FCSTD DOCUMENT  (FreeCAD 0.14R3703 (Git))
Label: halfHullS
License: CC-BY 3.0
LicenseURL: http://creativecommons.org/licenses/by/3.0/
objects: Sketcher::SketchObject×12, App::DocumentObjectGroup×1
note: 12 computed .brp shape members not serialized (recipe doc carries the construction recipe); baked Part::Feature solids carry a one-line shape summary decoded from their .brp

FEATURE [Sketcher::SketchObject] Sketch044  label="transomXY"
  sketch-geometry (3):
    g0: LineSegment StartX=0.095576 StartY=-850 StartZ=0 EndX=46.3737 EndY=-848.446 EndZ=0
    g1: LineSegment StartX=46.3737 StartY=-848.446 StartZ=0 EndX=77.9269 EndY=-843.772 EndZ=0
    g2: LineSegment StartX=77.9269 StartY=-843.772 StartZ=0 EndX=100 EndY=-839 EndZ=0
  constraints (5):
    c: Coincident(g0,g1)
    c: Coincident(g1,g2)
    c: DistanceY(g-1,g0) = -850
    c: DistanceY(g-1,g2) = -839
    c: DistanceX(g-1,g2) = 100
FEATURE [Sketcher::SketchObject] Sketch045  label="transom corners sketch"
  Placement = pos=(0,-828,43) rot=(1,0,0;1.71042rad)
  sketch-geometry (3):
    g0: LineSegment StartX=0 StartY=-34.8021 StartZ=0 EndX=45.4 EndY=-31.2923 EndZ=0
    g1: LineSegment StartX=45.4 StartY=-31.2923 StartZ=0 EndX=76.2 EndY=4.1704 EndZ=0
    g2: LineSegment StartX=76.2 StartY=4.1704 StartZ=0 EndX=100 EndY=75 EndZ=0
  constraints (6):
    c: Coincident(g0,g1)
    c: Coincident(g1,g2)
    c: DistanceX(g-1,g2) = 100
    c: DistanceY(g-1,g2) = 75
    c: DistanceX(g-1,g1) = 76.2
    c: DistanceX(g-1,g0) = 45.4
FEATURE [Sketcher::SketchObject] Sketch046  label="aft coachhouse cross-section sketch"
  Placement = pos=(0,-735,0) rot=(1,0,0;1.5708rad)
  sketch-geometry (3):
    g0: LineSegment StartX=0 StartY=-20.6602 StartZ=0 EndX=47.6 EndY=-7.7945 EndZ=0
    g1: LineSegment StartX=47.6 StartY=-7.7945 StartZ=0 EndX=96 EndY=34.1382 EndZ=0
    g2: LineSegment StartX=96 StartY=34.1382 StartZ=0 EndX=120 EndY=112 EndZ=0
  constraints (7):
    c: Coincident(g0,g1)
    c: Coincident(g1,g2)
    c: DistanceY(g-1,g2) = 112
    c: DistanceX(g-1,g2) = 120
    c: DistanceX(g-1,g1) = 96
    c: DistanceX(g-1,g0) = 0
    c: DistanceX(g-1,g0) = 47.6
FEATURE [Sketcher::SketchObject] Sketch047  label="mizzen mast cross-section sketch"
  Placement = pos=(0,-575,0) rot=(1,0,0;1.5708rad)
  sketch-geometry (3):
    g0: LineSegment StartX=0 StartY=-53.1503 StartZ=0 EndX=48 EndY=-36.6567 EndZ=0
    g1: LineSegment StartX=48 StartY=-36.6567 StartZ=0 EndX=126 EndY=14.6915 EndZ=0
    g2: LineSegment StartX=126 StartY=14.6915 StartZ=0 EndX=150 EndY=108 EndZ=0
  constraints (7):
    c: Coincident(g0,g1)
    c: Coincident(g1,g2)
    c: DistanceY(g-1,g2) = 108
    c: DistanceX(g-1,g2) = 150
    c: DistanceX(g-1,g1) = 126
    c: DistanceX(g-1,g0) = 48
    c: DistanceX(g-1,g0) = 0
FEATURE [Sketcher::SketchObject] Sketch  label="companionway cross-section sketch"
  Placement = pos=(0,-350,0) rot=(1,0,0;1.5708rad)
  sketch-geometry (3):
    g0: LineSegment StartX=0.336076 StartY=-63.7722 StartZ=0 EndX=116 EndY=-39.725 EndZ=0
    g1: LineSegment StartX=116 StartY=-39.725 StartZ=0 EndX=160 EndY=7.33871 EndZ=0
    g2: LineSegment StartX=160 StartY=7.33871 StartZ=0 EndX=170 EndY=110 EndZ=0
  constraints (6):
    c: Coincident(g0,g1)
    c: Coincident(g1,g2)
    c: DistanceY(g-1,g2) = 110
    c: DistanceX(g-1,g2) = 170
    c: DistanceX(g-1,g1) = 160
    c: DistanceX(g-1,g0) = 116
FEATURE [Sketcher::SketchObject] Sketch048  label="saloon cross-section sketch"
  Placement = pos=(0,-210,0) rot=(1,0,0;1.5708rad)
  sketch-geometry (3):
    g0: LineSegment StartX=0 StartY=-63.3729 StartZ=0 EndX=116 EndY=-39.32 EndZ=0
    g1: LineSegment StartX=116 StartY=-39.32 StartZ=0 EndX=160 EndY=7.49728 EndZ=0
    g2: LineSegment StartX=160 StartY=7.49728 StartZ=0 EndX=170 EndY=113 EndZ=0
  constraints (7):
    c: Coincident(g0,g1)
    c: Coincident(g1,g2)
    c: DistanceX(g-1,g2) = 170
    c: DistanceY(g-1,g2) = 113
    c: DistanceX(g-1,g1) = 160
    c: DistanceX(g-1,g0) = 116
    c: DistanceX(g-1,g0) = 0
FEATURE [Sketcher::SketchObject] Sketch049  label="main mast cross-section sketch"
  Placement = pos=(0,0,0) rot=(1,0,0;1.5708rad)
  sketch-geometry (3):
    g0: LineSegment StartX=0 StartY=-63.7463 StartZ=0 EndX=72 EndY=-39.956 EndZ=0
    g1: LineSegment StartX=72 StartY=-39.956 StartZ=0 EndX=126 EndY=8.30431 EndZ=0
    g2: LineSegment StartX=126 StartY=8.30431 StartZ=0 EndX=150 EndY=124 EndZ=0
  constraints (7):
    c: Coincident(g0,g1)
    c: Coincident(g1,g2)
    c: DistanceX(g-1,g0) = 0
    c: DistanceX(g-1,g0) = 72
    c: DistanceX(g-1,g1) = 126
    c: DistanceX(g-1,g2) = 150
    c: DistanceY(g-1,g2) = 124
FEATURE [Sketcher::SketchObject] Sketch050  label="forepeak cross-section sketch"
  Placement = pos=(0,100,0) rot=(1,0,0;1.5708rad)
  sketch-geometry (3):
    g0: LineSegment StartX=0 StartY=-55.9951 StartZ=0 EndX=52 EndY=-37.5826 EndZ=0
    g1: LineSegment StartX=52 StartY=-37.5826 StartZ=0 EndX=100 EndY=8.90891 EndZ=0
    g2: LineSegment StartX=100 StartY=8.90891 StartZ=0 EndX=125 EndY=130 EndZ=0
  constraints (7):
    c: Coincident(g0,g1)
    c: Coincident(g1,g2)
    c: DistanceX(g-1,g0) = 0
    c: DistanceX(g-1,g0) = 52
    c: DistanceX(g-1,g1) = 100
    c: DistanceX(g-1,g2) = 125
    c: DistanceY(g-1,g2) = 130
FEATURE [Sketcher::SketchObject] Sketch051  label="for coachhouse cross-section sketch"
  Placement = pos=(0,155,0) rot=(1,0,0;1.5708rad)
  sketch-geometry (3):
    g0: LineSegment StartX=0 StartY=-51.2168 StartZ=0 EndX=40 EndY=-32.2513 EndZ=0
    g1: LineSegment StartX=40 StartY=-32.2513 StartZ=0 EndX=85 EndY=10.574 EndZ=0
    g2: LineSegment StartX=85 StartY=10.574 StartZ=0 EndX=110 EndY=135 EndZ=0
  constraints (7):
    c: Coincident(g0,g1)
    c: Coincident(g1,g2)
    c: DistanceX(g-1,g0) = 0
    c: DistanceX(g-1,g0) = 40
    c: DistanceX(g-1,g1) = 85
    c: DistanceX(g-1,g2) = 110
    c: DistanceY(g-1,g2) = 135
FEATURE [Sketcher::SketchObject] Sketch052  label="mid forepeak cross-section sketch"
  Placement = pos=(0,235,0) rot=(1,0,0;1.5708rad)
  sketch-geometry (3):
    g0: LineSegment StartX=0 StartY=-33.4528 StartZ=0 EndX=25 EndY=-15.1481 EndZ=0
    g1: LineSegment StartX=25 StartY=-15.1481 StartZ=0 EndX=65 EndY=32.6627 EndZ=0
    g2: LineSegment StartX=65 StartY=32.6627 StartZ=0 EndX=80 EndY=142 EndZ=0
  constraints (7):
    c: Coincident(g0,g1)
    c: Coincident(g1,g2)
    c: DistanceX(g-1,g0) = 0
    c: DistanceX(g-1,g0) = 25
    c: DistanceX(g-1,g1) = 65
    c: DistanceX(g-1,g2) = 80
    c: DistanceY(g-1,g2) = 142
FEATURE [Sketcher::SketchObject] Sketch053  label="anchor locker cross-section sketch"
  Placement = pos=(0,300,0) rot=(1,0,0;1.5708rad)
  sketch-geometry (3):
    g0: LineSegment StartX=0 StartY=17.5261 StartZ=0 EndX=18.8 EndY=33.7851 EndZ=0
    g1: LineSegment StartX=18.8 StartY=33.7851 StartZ=0 EndX=38.8 EndY=74.1314 EndZ=0
    g2: LineSegment StartX=38.8 StartY=74.1314 StartZ=0 EndX=55 EndY=150 EndZ=0
  constraints (7):
    c: Coincident(g0,g1)
    c: Coincident(g1,g2)
    c: DistanceX(g-1,g0) = 0
    c: DistanceX(g-1,g0) = 18.8
    c: DistanceX(g-1,g1) = 38.8
    c: DistanceX(g-1,g2) = 55
    c: DistanceY(g-1,g2) = 150
FEATURE [Sketcher::SketchObject] Sketch054  label="stemline sketch"
  Placement = pos=(0,0,0) rot=(0.57735,0.57735,0.57735;2.0944rad)
  sketch-geometry (3):
    g0: LineSegment StartX=300 StartY=16.7391 StartZ=0 EndX=332.509 EndY=58.7967 EndZ=0
    g1: LineSegment StartX=332.509 StartY=58.7967 StartZ=0 EndX=370.125 EndY=115.234 EndZ=0
    g2: LineSegment StartX=370.125 StartY=115.234 StartZ=0 EndX=396.961 EndY=163.122 EndZ=0
  constraints (3):
    c: Coincident(g0,g1)
    c: Coincident(g1,g2)
    c: DistanceX(g-1,g0) = 300
FEATURE [App::DocumentObjectGroup] Group  label="hull"
  Group = -> [Sketch044,Sketch045,Sketch046,Sketch047,Sketch,Sketch048,Sketch049,Sketch050,Sketch051,Sketch052,Sketch053,Sketch054]
